# Revit family: Legrand Caja Plexo³ 2 módulos
name_source: partatom
category: Equipement électrique
revit_build: Autodesk Revit 2018 (Build: 20170223_1515(x64)
units: mm (PartAtom-declared; Revit-internal decimal feet)

## family parameters
Basée sur le plan de construction = Non
Configuration du panneau = Deux colonnes, circuits au sein
Cote de connecteur circulaire = Utiliser le diamètre
Couper avec des vides une fois chargée = Non
Numéro OmniClass = 23.80.30.11.17
Partagée = Non
Point de calcul de pièce = Non
Titre OmniClass = Distribution Boards and Control Panels
Toujours verticalement = Oui
Type d'élément = Tableau de raccordement

## types (2) — shared parameters
Condiciones Generales de Uso = https://export.legrand.com
Fabricant = Legrand
IK = 09
IP = 65
Image du type = plexo3_1_rangee_001902_pw_234841_pz_2.jpg
Materia = Poliestireno
RAL = 7046
URL = www.legrand.fr

## per-type parameters (varying)
| type | Caja 001902 | Caja 601932 |
| Plexo³ 2 módulos de 1 fila  001902 | Oui | Non |
| Plexo³ 2 módulos de 1 fila  601932 | Non | Oui |

note: column(s) folded — value = type name in every type: Description
